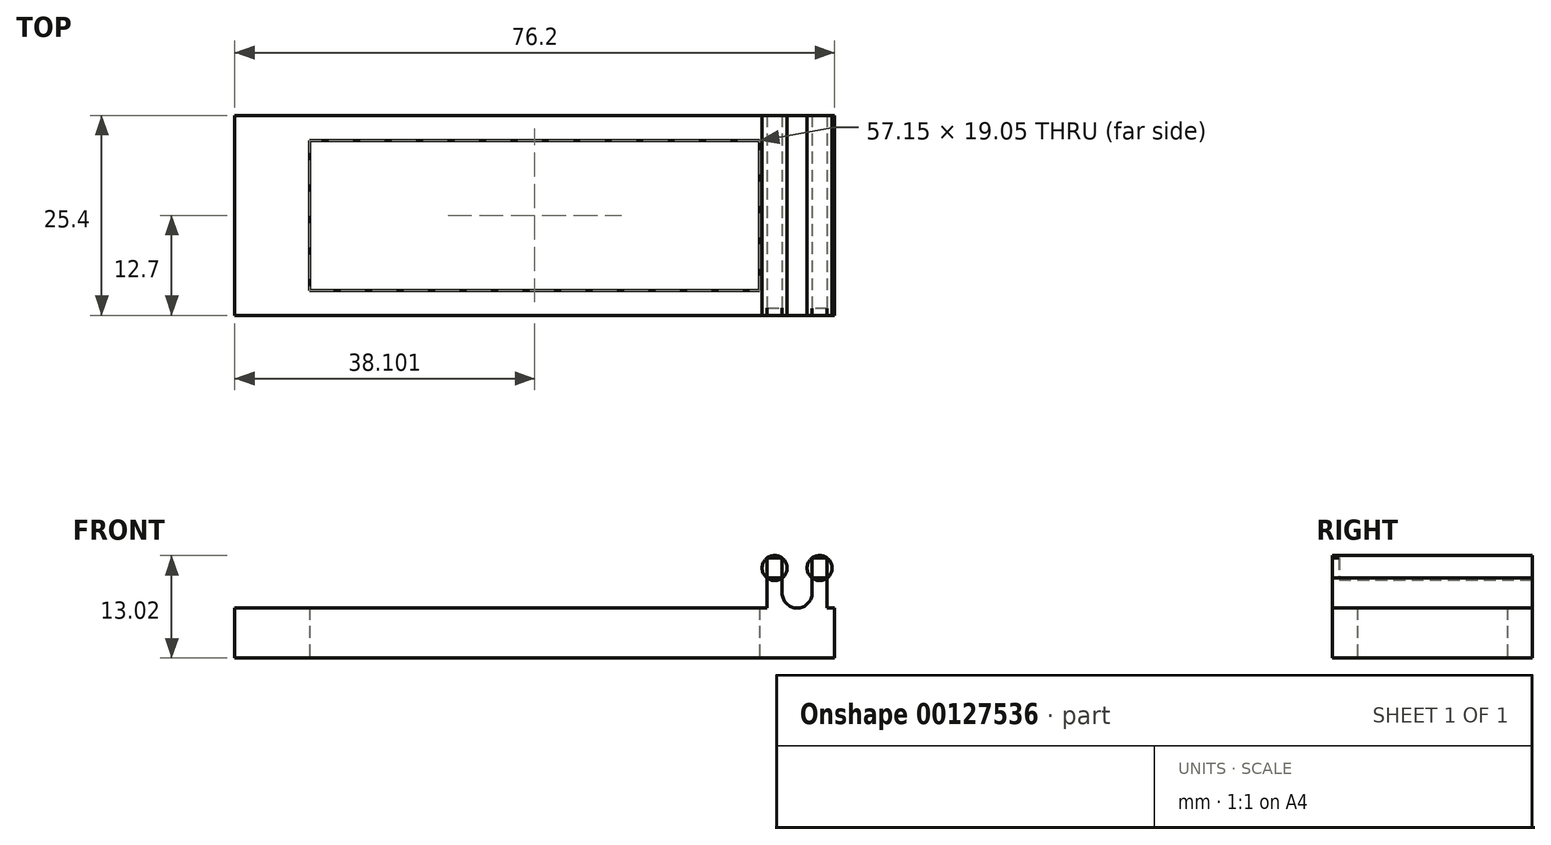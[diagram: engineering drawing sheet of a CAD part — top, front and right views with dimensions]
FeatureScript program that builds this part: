
annotation { "Feature Type Name" : "Feature", "Feature Type Description" : "" }
export const myFeature = defineFeature(function(context is Context, id is Id, definition is map)
    precondition{}
    {
        {
            var Q0;
            Q0=qCreatedBy(makeId("Top.planeOp"),FACE);
            var sketch = newSketch(context, id + "F0", { "sketchPlane" : qUnion([Q0])});
            skLineSegment(sketch, "E0.bottom", {"start": v(-10.5, 28.65) * mm, "end": v(65.7, 28.65) * mm});
            skLineSegment(sketch, "E0.top", {"start": v(-10.5, 3.25) * mm, "end": v(65.7, 3.25) * mm});
            skLineSegment(sketch, "E0.left", {"start": v(-10.5, 28.65) * mm, "end": v(-10.5, 3.25) * mm});
            skLineSegment(sketch, "E0.right", {"start": v(65.7, 28.65) * mm, "end": v(65.7, 3.25) * mm});
            skLineSegment(sketch, "E1.bottom", {"start": v(56.17, 6.43) * mm, "end": v(-0.98, 6.43) * mm});
            skLineSegment(sketch, "E1.top", {"start": v(56.17, 25.48) * mm, "end": v(-0.98, 25.48) * mm});
            skLineSegment(sketch, "E1.left", {"start": v(56.17, 6.43) * mm, "end": v(56.17, 25.48) * mm});
            skLineSegment(sketch, "E1.right", {"start": v(-0.98, 6.43) * mm, "end": v(-0.98, 25.48) * mm});
            skPoint(sketch, "E1.middle", {"position": v(27.6, 15.95) * mm});
            skPoint(sketch, "E1.middle.positionSnap0", {"position": v(65.7, 15.95) * mm});
            skPoint(sketch, "E1.middle.positionSnap1", {"position": v(27.6, 28.65) * mm});
            skPoint(sketch, "E1.centerSnap0", {"position": v(65.7, 15.95) * mm});
            skPoint(sketch, "E1.centerSnap1", {"position": v(27.6, 28.65) * mm});
            skSolve(sketch);
        }
        {
            var Q0;
            Q0 = qSketchRegion(id + "F0", true);
            extrude(context, id + "F1", {"entities" : qUnion([Q0]), "depth" : 6.35 * mm});
        }
        {
            var Q0;
            Q0=makeQuery(id+"F1.opExtrude","CAP_FACE",FACE,{"disambiguationData":[OSD([sQuery(id+"F0.wireOp",EDGE,"E0.bottom"),sQuery(id+"F0.wireOp",EDGE,"E0.top"),sQuery(id+"F0.wireOp",EDGE,"E0.left"),sQuery(id+"F0.wireOp",EDGE,"E0.right"),sQuery(id+"F0.wireOp",EDGE,"E1.bottom"),sQuery(id+"F0.wireOp",EDGE,"E1.top"),sQuery(id+"F0.wireOp",EDGE,"E1.left"),sQuery(id+"F0.wireOp",EDGE,"E1.right")])],"isStart":false});
            var sketch = newSketch(context, id + "F2", { "sketchPlane" : qUnion([Q0])});
            skSolve(sketch);
        }
        {
            var Q0;
            Q0=makeQuery(id+"F2.imprint","IMPRINT",FACE,{"disambiguationData":[TD([[makeQuery(id+"F2.imprint","IMPRINT",EDGE,{"derivedFrom":makeQuery(id+"F1.opExtrude","CAP_EDGE",EDGE,{"disambiguationData":[OSD([sQuery(id+"F0.wireOp",EDGE,"E0.bottom")])],"isStart":false})}),-1.0]])]});
            var sketch = newSketch(context, id + "F3", { "sketchPlane" : qUnion([Q0])});
            skLineSegment(sketch, "E2.0", {"start": v(65.7, 28.65) * mm, "end": v(65.7, 3.25) * mm});
            skLineSegment(sketch, "E3.0", {"start": v(-10.5, 28.65) * mm, "end": v(65.7, 28.65) * mm});
            skLineSegment(sketch, "E4.0", {"start": v(56.17, 6.43) * mm, "end": v(56.17, 25.48) * mm});
            skLineSegment(sketch, "E5", {"start": v(65.7, 28.65) * mm, "end": v(56.17, 28.65) * mm});
            skLineSegment(sketch, "E6.bottom", {"start": v(64.74, 28.65) * mm, "end": v(57.12, 28.65) * mm});
            skLineSegment(sketch, "E6.top", {"start": v(64.74, 3.25) * mm, "end": v(57.12, 3.25) * mm});
            skLineSegment(sketch, "E6.left", {"start": v(64.74, 28.65) * mm, "end": v(64.74, 3.25) * mm});
            skLineSegment(sketch, "E6.right", {"start": v(57.12, 28.65) * mm, "end": v(57.12, 3.25) * mm});
            skPoint(sketch, "E6.middle", {"position": v(60.93, 15.95) * mm});
            skPoint(sketch, "E6.middle.positionSnap0", {"position": v(65.7, 15.95) * mm});
            skPoint(sketch, "E6.middle.positionSnap1", {"position": v(60.93, 28.65) * mm});
            skPoint(sketch, "E6.centerSnap0", {"position": v(65.7, 15.95) * mm});
            skPoint(sketch, "E6.centerSnap1", {"position": v(60.93, 28.65) * mm});
            skLineSegment(sketch, "E7.bottom", {"start": v(62.83, 28.65) * mm, "end": v(59.02, 28.65) * mm});
            skLineSegment(sketch, "E7.top", {"start": v(62.83, 3.25) * mm, "end": v(59.02, 3.25) * mm});
            skLineSegment(sketch, "E7.left", {"start": v(62.83, 28.65) * mm, "end": v(62.83, 3.25) * mm});
            skLineSegment(sketch, "E7.right", {"start": v(59.02, 28.65) * mm, "end": v(59.02, 3.25) * mm});
            skSolve(sketch);
        }
        {
            var Q0;
            {var subQ0=sQuery(id+"F3.wireOp",EDGE,"E6.right");Q0=makeQuery(id+"F3.imprint","IMPRINT",FACE,{"disambiguationData":[TD([[makeQuery(id+"F3.imprint","IMPRINT",EDGE,{"derivedFrom":subQ0}),1.0]])]});}
            var Q1;
            {var subQ0=sQuery(id+"F3.wireOp",EDGE,"E6.left");Q1=makeQuery(id+"F3.imprint","IMPRINT",FACE,{"disambiguationData":[TD([[makeQuery(id+"F3.imprint","IMPRINT",EDGE,{"derivedFrom":subQ0}),-1.0]])]});}
            extrude(context, id + "F4", {"entities" : qUnion([Q0, Q1]), "operationType" : NewBodyOperationType.ADD, "depth" : 3.8 * mm});
        }
        {
            var Q0;
            Q0=makeQuery(id+"F4.opExtrude","CAP_EDGE",EDGE,{"disambiguationData":[OSD([sQuery(id+"F3.wireOp",EDGE,"E7.right")])],"isStart":true});
            var Q1;
            Q1=makeQuery(id+"F4.opExtrude","CAP_EDGE",EDGE,{"disambiguationData":[OSD([sQuery(id+"F3.wireOp",EDGE,"E7.left")])],"isStart":true});
            fillet(context, id + "F5", {"entities" : qUnion([Q0, Q1]), "radius" : 1.9 * mm, "tangentPropagation" : true, "allowEdgeOverflow" : false});
        }
        {
            var Q0;
            Q0=makeQuery(id+"F4.opExtrude","CAP_FACE",FACE,{"disambiguationData":[OSD([sQuery(id+"F3.wireOp",EDGE,"E6.bottom"),sQuery(id+"F3.wireOp",EDGE,"E6.top"),sQuery(id+"F3.wireOp",EDGE,"E6.left"),sQuery(id+"F3.wireOp",EDGE,"E7.left")])],"isStart":false});
            var sketch = newSketch(context, id + "F6", { "sketchPlane" : qUnion([Q0])});
            skLineSegment(sketch, "E8.bottom", {"start": v(64.74, 3.25) * mm, "end": v(62.83, 3.25) * mm});
            skLineSegment(sketch, "E8.top", {"start": v(64.74, 4.1) * mm, "end": v(62.83, 4.1) * mm});
            skLineSegment(sketch, "E8.left", {"start": v(64.74, 3.25) * mm, "end": v(64.74, 4.1) * mm});
            skLineSegment(sketch, "E8.right", {"start": v(62.83, 3.25) * mm, "end": v(62.83, 4.1) * mm});
            skSolve(sketch);
        }
        {
            var Q0;
            Q0 = qSketchRegion(id + "F6", true);
            extrude(context, id + "F7", {"entities" : qUnion([Q0]), "depth" : 2.54 * mm});
        }
        {
            var Q0;
            Q0=makeQuery(id+"F7.opExtrude","SWEPT_FACE",FACE,{"disambiguationData":[OSD([sQuery(id+"F6.wireOp",EDGE,"E8.bottom")])]});
            var sketch = newSketch(context, id + "F8", { "sketchPlane" : qUnion([Q0])});
            skCircle(sketch, "E9", {"center": v(63.79, 11.43) * mm, "radius": 1.59 * mm});
            skPoint(sketch, "E9.centerSnap0", {"position": v(64.74, 11.43) * mm});
            skPoint(sketch, "E9.centerSnap1", {"position": v(63.79, 12.7) * mm});
            skSolve(sketch);
        }
        {
            var Q0;
            Q0 = qSketchRegion(id + "F8", true);
            var Q1;
            {var subQ0=sQuery(id+"F3.wireOp",EDGE,"E6.bottom");var subQ1=sQuery(id+"F3.wireOp",EDGE,"E5");Q1=makeQuery(id+"F4.boolean.opBoolean","MERGE",FACE,{"derivedFrom":[makeQuery(id+"F1.opExtrude","SWEPT_FACE",FACE,{"disambiguationData":[OSD([sQuery(id+"F0.wireOp",EDGE,"E0.bottom")])]}),makeQuery(id+"F4.opExtrude","SWEPT_FACE",FACE,{"disambiguationData":[OSD([subQ0]),TDD([makeQuery(id+"F3.imprint","IMPRINT",EDGE,{"disambiguationData":[TD([[makeQuery(id+"F3.imprint","INTERSECT",VERTEX,{"derivedFrom":[subQ1,subQ0,sQuery(id+"F3.wireOp",EDGE,"E6.right")]}),-1.0]])],"derivedFrom":subQ0})])]}),makeQuery(id+"F4.opExtrude","SWEPT_FACE",FACE,{"disambiguationData":[OSD([subQ0]),TDD([makeQuery(id+"F3.imprint","IMPRINT",EDGE,{"disambiguationData":[TD([[makeQuery(id+"F3.imprint","INTERSECT",VERTEX,{"derivedFrom":[subQ1,subQ0,sQuery(id+"F3.wireOp",EDGE,"E6.left")]}),1.0]])],"derivedFrom":subQ0})])]})]});}
            extrude(context, id + "F9", {"entities" : qUnion([Q0]), "endBound" : BoundingType.UP_TO_SURFACE, "oppositeDirection" : true, "endBoundEntityFace" : qUnion([Q1]), "depth" : 25.4 * mm});
        }
        {
            var Q0;
            Q0=makeQuery(id+"F4.opExtrude","CAP_FACE",FACE,{"disambiguationData":[OSD([sQuery(id+"F3.wireOp",EDGE,"E6.bottom"),sQuery(id+"F3.wireOp",EDGE,"E6.top"),sQuery(id+"F3.wireOp",EDGE,"E6.right"),sQuery(id+"F3.wireOp",EDGE,"E7.right")])],"isStart":false});
            var sketch = newSketch(context, id + "F10", { "sketchPlane" : qUnion([Q0])});
            skLineSegment(sketch, "E10.bottom", {"start": v(57.12, 3.25) * mm, "end": v(59.02, 3.25) * mm});
            skLineSegment(sketch, "E10.top", {"start": v(57.12, 4.2) * mm, "end": v(59.02, 4.2) * mm});
            skLineSegment(sketch, "E10.left", {"start": v(57.12, 3.25) * mm, "end": v(57.12, 4.2) * mm});
            skLineSegment(sketch, "E10.right", {"start": v(59.02, 3.25) * mm, "end": v(59.02, 4.2) * mm});
            skSolve(sketch);
        }
        {
            var Q0;
            Q0 = qSketchRegion(id + "F10", true);
            extrude(context, id + "F11", {"entities" : qUnion([Q0]), "depth" : 2.54 * mm});
        }
        {
            var Q0;
            Q0=makeQuery(id+"F11.opExtrude","SWEPT_FACE",FACE,{"disambiguationData":[OSD([sQuery(id+"F10.wireOp",EDGE,"E10.bottom")])]});
            var sketch = newSketch(context, id + "F12", { "sketchPlane" : qUnion([Q0])});
            skCircle(sketch, "E11", {"center": v(58.07, 11.43) * mm, "radius": 1.59 * mm});
            skPoint(sketch, "E11.centerSnap0", {"position": v(59.02, 11.43) * mm});
            skPoint(sketch, "E11.centerSnap1", {"position": v(58.07, 12.7) * mm});
            skSolve(sketch);
        }
        {
            var Q0;
            Q0 = qSketchRegion(id + "F12", true);
            var Q1;
            {var subQ0=sQuery(id+"F3.wireOp",EDGE,"E6.bottom");var subQ1=sQuery(id+"F3.wireOp",EDGE,"E5");Q1=makeQuery(id+"F4.boolean.opBoolean","MERGE",FACE,{"derivedFrom":[makeQuery(id+"F1.opExtrude","SWEPT_FACE",FACE,{"disambiguationData":[OSD([sQuery(id+"F0.wireOp",EDGE,"E0.bottom")])]}),makeQuery(id+"F4.opExtrude","SWEPT_FACE",FACE,{"disambiguationData":[OSD([subQ0]),TDD([makeQuery(id+"F3.imprint","IMPRINT",EDGE,{"disambiguationData":[TD([[makeQuery(id+"F3.imprint","INTERSECT",VERTEX,{"derivedFrom":[subQ1,subQ0,sQuery(id+"F3.wireOp",EDGE,"E6.right")]}),-1.0]])],"derivedFrom":subQ0})])]}),makeQuery(id+"F4.opExtrude","SWEPT_FACE",FACE,{"disambiguationData":[OSD([subQ0]),TDD([makeQuery(id+"F3.imprint","IMPRINT",EDGE,{"disambiguationData":[TD([[makeQuery(id+"F3.imprint","INTERSECT",VERTEX,{"derivedFrom":[subQ1,subQ0,sQuery(id+"F3.wireOp",EDGE,"E6.left")]}),1.0]])],"derivedFrom":subQ0})])]})]});}
            extrude(context, id + "F13", {"entities" : qUnion([Q0]), "endBound" : BoundingType.UP_TO_SURFACE, "oppositeDirection" : true, "endBoundEntityFace" : qUnion([Q1]), "depth" : 25.4 * mm});
        }
    });
